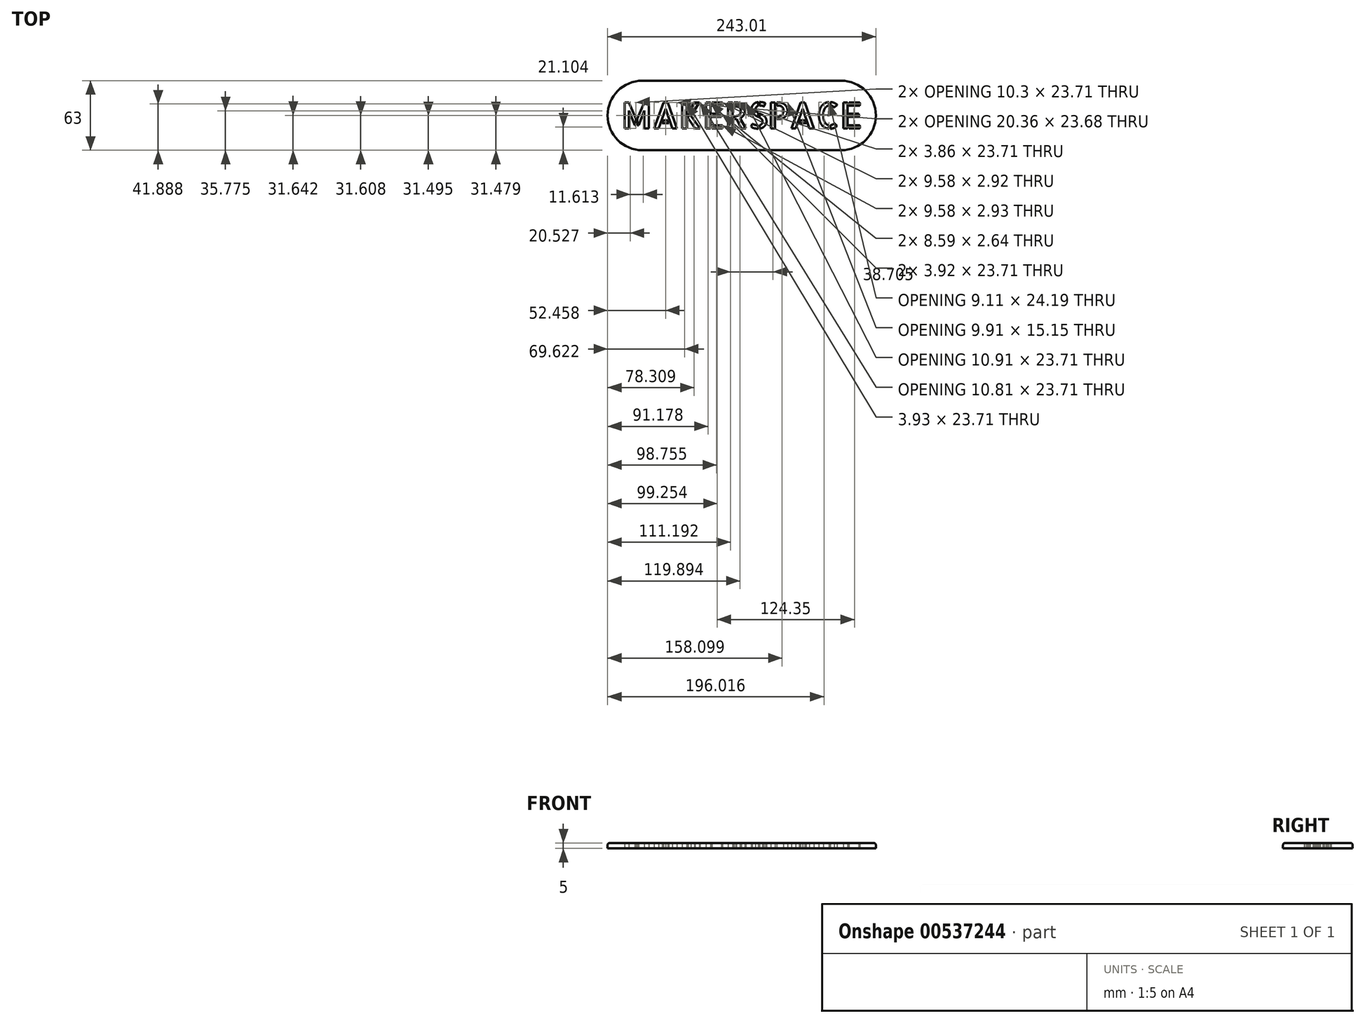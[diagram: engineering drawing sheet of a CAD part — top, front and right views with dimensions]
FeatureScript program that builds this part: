
annotation { "Feature Type Name" : "Feature", "Feature Type Description" : "" }
export const myFeature = defineFeature(function(context is Context, id is Id, definition is map)
    precondition{}
    {
        {
            var Q0;
            Q0=qCreatedBy(makeId("Top.planeOp"),FACE);
            var sketch = newSketch(context, id + "F0", { "sketchPlane" : qUnion([Q0])});
            skText(sketch, "E0", { "text": "MAKERSPACE", "fontName": "AllertaStencil-Regular.ttf"});
            skLineSegment(sketch, "E1.bottom", {"start": v(199.09, -43.36) * mm, "end": v(19.09, -43.36) * mm});
            skLineSegment(sketch, "E1.top", {"start": v(199.09, 19.64) * mm, "end": v(19.09, 19.64) * mm});
            skLineSegment(sketch, "E1.left", {"start": v(199.09, -43.36) * mm, "end": v(199.09, 19.64) * mm});
            skLineSegment(sketch, "E1.right", {"start": v(19.09, -43.36) * mm, "end": v(19.09, 19.64) * mm});
            skPoint(sketch, "E1.middle", {"position": v(109.09, -11.86) * mm});
            skArc(sketch, "E2", {"start": v(19.09, 19.64) * mm, "mid": v(-12.42, -11.86) * mm, "end": v(19.09, -43.36) * mm});
            skArc(sketch, "E3", {"start": v(199.09, -43.36) * mm, "mid": v(230.59, -11.86) * mm, "end": v(199.09, 19.64) * mm});
            const initialGuessF0  = {"E0": [0, -0.02372, 1, 0, 0.02372]};
            skSetInitialGuess(sketch, initialGuessF0);
            skSolve(sketch);
        }
        {
            var Q0;
            Q0=makeQuery(id+"F0.imprint","IMPRINT",FACE,{"disambiguationData":[TD([[makeQuery(id+"F0.imprint","IMPRINT",EDGE,{"derivedFrom":sQuery(id+"F0.wireOp",EDGE,"E0.sketch_text.stroke-0")}),1.0]])]});
            var Q1;
            {var subQ9=sQuery(id+"F0.wireOp",EDGE,"E0.sketch_text.stroke-8");Q1=makeQuery(id+"F0.imprint","IMPRINT",FACE,{"disambiguationData":[TD([[makeQuery(id+"F0.imprint","IMPRINT",EDGE,{"derivedFrom":subQ9}),1.0]])]});}
            var Q2;
            Q2=makeQuery(id+"F0.imprint","IMPRINT",FACE,{"disambiguationData":[TD([[makeQuery(id+"F0.imprint","IMPRINT",EDGE,{"derivedFrom":sQuery(id+"F0.wireOp",EDGE,"E0.sketch_text.stroke-200")}),1.0]])]});
            extrude(context, id + "F1", {"entities" : qUnion([Q0, Q1, Q2]), "depth" : 5 * mm, "offsetDistance" : 25 * mm});
        }
        {
            var Q0;
            Q0=makeQuery(id+"F1.opExtrude","CAP_EDGE",EDGE,{"disambiguationData":[OSD([sQuery(id+"F0.wireOp",EDGE,"E1.bottom")])],"isStart":false});
            fillet(context, id + "F2", {"entities" : qUnion([Q0]), "radius" : 2 * mm, "tangentPropagation" : true, "allowEdgeOverflow" : false});
        }
    });
